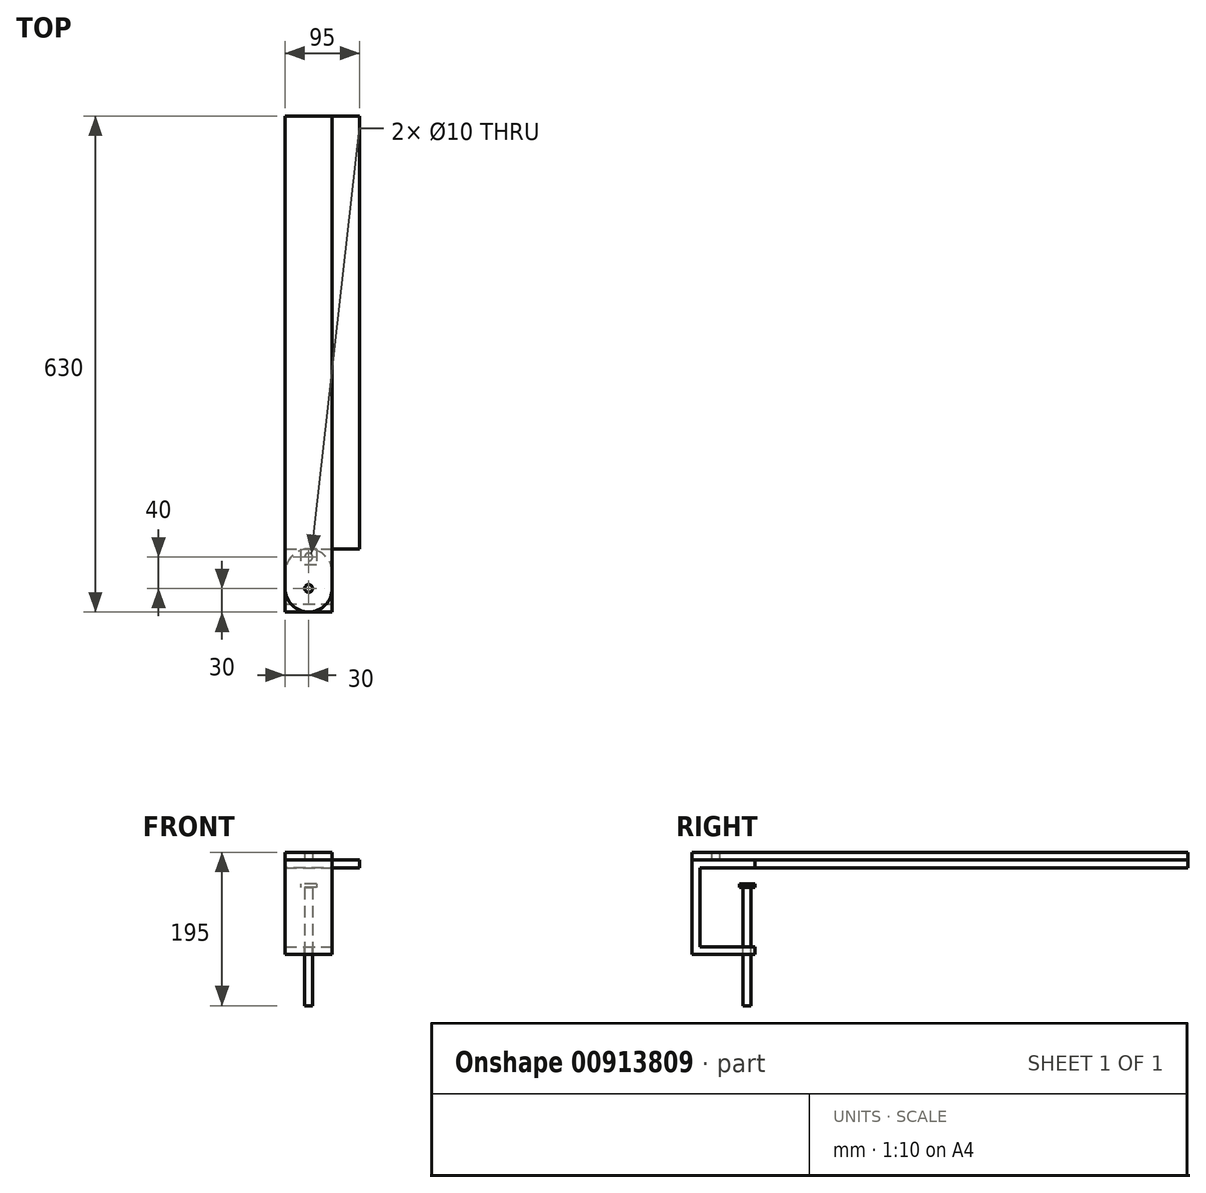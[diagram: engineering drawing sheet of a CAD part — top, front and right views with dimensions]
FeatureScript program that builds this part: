
annotation { "Feature Type Name" : "Feature", "Feature Type Description" : "" }
export const myFeature = defineFeature(function(context is Context, id is Id, definition is map)
    precondition{}
    {
        {
            assignVariable(context, id + "F0", {"name" : "espessura", "anyValue" : 10});
        }
        {
            var Q0;
            Q0=qCreatedBy(makeId("Top.planeOp"),FACE);
            var sketch = newSketch(context, id + "F1", { "sketchPlane" : qUnion([Q0])});
            skLineSegment(sketch, "E0.bottom", {"start": v(0, 0) * mm, "end": v(35, 0) * mm});
            skLineSegment(sketch, "E0.top", {"start": v(0, 550) * mm, "end": v(35, 550) * mm});
            skLineSegment(sketch, "E0.left", {"start": v(0, 0) * mm, "end": v(0, 550) * mm});
            skLineSegment(sketch, "E0.right", {"start": v(35, 0) * mm, "end": v(35, 550) * mm});
            skLineSegment(sketch, "E1.top", {"start": v(0, 550) * mm, "end": v(-60, 550) * mm});
            skLineSegment(sketch, "E1.right", {"start": v(-60, 0) * mm, "end": v(-60, 550) * mm});
            skLineSegment(sketch, "E2.top", {"start": v(-60, -50) * mm, "end": v(0, -50) * mm, "construction": true});
            skLineSegment(sketch, "E2.left", {"start": v(-60, 0) * mm, "end": v(-60, -50) * mm});
            skLineSegment(sketch, "E2.right", {"start": v(0, 0) * mm, "end": v(0, -50) * mm});
            skArc(sketch, "E3", {"start": v(-60, -50) * mm, "mid": v(-30, -80) * mm, "end": v(0, -50) * mm});
            skCircle(sketch, "E4", {"center": v(-30, -50) * mm, "radius": 5 * mm});
            skLineSegment(sketch, "E5", {"start": v(-60, 0) * mm, "end": v(0, 0) * mm});
            skSolve(sketch);
        }
        {
            var Q0;
            Q0=makeQuery(id+"F1.imprint","IMPRINT",FACE,{"disambiguationData":[TD([[makeQuery(id+"F1.imprint","IMPRINT",EDGE,{"derivedFrom":sQuery(id+"F1.wireOp",EDGE,"E1.top")}),1.0]])]});
            extrude(context, id + "F2", {"entities" : qUnion([Q0]), "depth" : (2 * getVariable(context, 'espessura')) * mm});
        }
        {
            var Q0;
            Q0=makeQuery(id+"F1.imprint","IMPRINT",FACE,{"disambiguationData":[TD([[makeQuery(id+"F1.imprint","IMPRINT",EDGE,{"derivedFrom":sQuery(id+"F1.wireOp",EDGE,"E0.bottom")}),1.0]])]});
            extrude(context, id + "F3", {"entities" : qUnion([Q0]), "operationType" : NewBodyOperationType.ADD, "depth" : (getVariable(context, 'espessura')) * mm});
        }
        {
            var Q0;
            Q0=makeQuery(id+"F1.imprint","IMPRINT",FACE,{"disambiguationData":[TD([[makeQuery(id+"F1.imprint","IMPRINT",EDGE,{"derivedFrom":sQuery(id+"F1.wireOp",EDGE,"E2.left")}),1.0]])]});
            extrude(context, id + "F4", {"entities" : qUnion([Q0]), "operationType" : NewBodyOperationType.ADD, "depth" : (2 * getVariable(context, 'espessura')) * mm});
        }
        {
            var Q0;
            Q0=makeQuery(id+"F1.imprint","IMPRINT",FACE,{"disambiguationData":[TD([[makeQuery(id+"F1.imprint","IMPRINT",EDGE,{"derivedFrom":sQuery(id+"F1.wireOp",EDGE,"E2.left")}),1.0]])]});
            extrude(context, id + "F5", {"entities" : qUnion([Q0]), "operationType" : NewBodyOperationType.REMOVE, "oppositeDirection" : true, "depth" : -(getVariable(context, 'espessura')) * mm});
        }
        {
            var Q0;
            {var subQ0=sQuery(id+"F1.wireOp",EDGE,"E5");var subQ1=sQuery(id+"F1.wireOp",EDGE,"E0.left");Q0=makeQuery(id+"F4.boolean.opBoolean","MERGE",FACE,{"derivedFrom":[makeQuery(id+"F3.boolean.opBoolean","MERGE",FACE,{"derivedFrom":[makeQuery(id+"F2.opExtrude","CAP_FACE",FACE,{"disambiguationData":[OSD([sQuery(id+"F1.wireOp",EDGE,"E1.top"),subQ1,sQuery(id+"F1.wireOp",EDGE,"E1.right"),subQ0])],"isStart":true}),makeQuery(id+"F3.opExtrude","CAP_FACE",FACE,{"disambiguationData":[OSD([sQuery(id+"F1.wireOp",EDGE,"E0.bottom"),sQuery(id+"F1.wireOp",EDGE,"E0.top"),sQuery(id+"F1.wireOp",EDGE,"E0.right"),subQ1])],"isStart":true})]}),makeQuery(id+"F4.opExtrude","CAP_FACE",FACE,{"disambiguationData":[OSD([sQuery(id+"F1.wireOp",EDGE,"E2.left"),sQuery(id+"F1.wireOp",EDGE,"E2.right"),sQuery(id+"F1.wireOp",EDGE,"E3"),sQuery(id+"F1.wireOp",EDGE,"E4"),subQ0])],"isStart":true})]});}
            var sketch = newSketch(context, id + "F6", { "sketchPlane" : qUnion([Q0])});
            skPoint(sketch, "E6.0", {"position": v(-60, 0) * mm});
            skPoint(sketch, "E7.0", {"position": v(0, 0) * mm});
            skLineSegment(sketch, "E8", {"start": v(-60, 0) * mm, "end": v(0, 0) * mm, "construction": true});
            skLineSegment(sketch, "E9", {"start": v(-30, 0) * mm, "end": v(-30, 30) * mm, "construction": true});
            skLineSegment(sketch, "E10", {"start": v(-60, 30) * mm, "end": v(-60, 30) * mm});
            skArc(sketch, "E11", {"start": v(-60, 30) * mm, "mid": v(-30, 0) * mm, "end": v(0, 30) * mm});
            skPoint(sketch, "E12.0", {"position": v(-30, 80) * mm});
            skPoint(sketch, "E13", {"position": v(-60, 30) * mm});
            skLineSegment(sketch, "E14.bottom", {"start": v(-60, 30) * mm, "end": v(0, 30) * mm, "construction": true});
            skLineSegment(sketch, "E14.top", {"start": v(-60, 80) * mm, "end": v(0, 80) * mm});
            skLineSegment(sketch, "E14.left", {"start": v(-60, 30) * mm, "end": v(-60, 80) * mm});
            skLineSegment(sketch, "E14.right", {"start": v(0, 30) * mm, "end": v(0, 80) * mm});
            skLineSegment(sketch, "E15", {"start": v(-60, 70) * mm, "end": v(0, 70) * mm});
            skSolve(sketch);
        }
        {
            var Q0;
            Q0=makeQuery(id+"F6.imprint","IMPRINT",FACE,{"disambiguationData":[TD([[makeQuery(id+"F6.imprint","IMPRINT",EDGE,{"derivedFrom":sQuery(id+"F6.wireOp",EDGE,"E14.top")}),-1.0]])]});
            var Q1;
            {var subQ3=sQuery(id+"F6.wireOp",EDGE,"E15");Q1=makeQuery(id+"F6.imprint","IMPRINT",FACE,{"disambiguationData":[TD([[makeQuery(id+"F6.imprint","IMPRINT",EDGE,{"derivedFrom":subQ3}),-1.0]])]});}
            extrude(context, id + "F7", {"entities" : qUnion([Q0, Q1]), "oppositeDirection" : true, "depth" : (getVariable(context, 'espessura')) * mm});
        }
        {
            var Q0;
            {var subQ0=sQuery(id+"F6.wireOp",EDGE,"E14.top");Q0=makeQuery(id+"F6.imprint","IMPRINT",FACE,{"disambiguationData":[TD([[makeQuery(id+"F6.imprint","IMPRINT",EDGE,{"derivedFrom":subQ0}),-1.0]])]});}
            extrude(context, id + "F8", {"entities" : qUnion([Q0]), "operationType" : NewBodyOperationType.ADD, "depth" : 100 * mm});
        }
        {
            var Q0;
            Q0=makeQuery(id+"F8.opExtrude","CAP_FACE",FACE,{"disambiguationData":[OSD([sQuery(id+"F6.wireOp",EDGE,"E14.top"),sQuery(id+"F6.wireOp",EDGE,"E14.left"),sQuery(id+"F6.wireOp",EDGE,"E14.right"),sQuery(id+"F6.wireOp",EDGE,"E15")])],"isStart":false});
            var sketch = newSketch(context, id + "F9", { "sketchPlane" : qUnion([Q0])});
            skLineSegment(sketch, "E16.0", {"start": v(-60, 80) * mm, "end": v(0, 80) * mm});
            skLineSegment(sketch, "E17.0.1", {"start": v(-60, 80) * mm, "end": v(-60, 70) * mm});
            skArc(sketch, "E17.0.2", {"start": v(-60, 30) * mm, "mid": v(-51.21, 8.79) * mm, "end": v(-30, 0) * mm});
            skArc(sketch, "E17.0.3", {"start": v(-30, 0) * mm, "mid": v(-8.79, 8.79) * mm, "end": v(0, 30) * mm});
            skLineSegment(sketch, "E17.0.4", {"start": v(0, 30) * mm, "end": v(0, 70) * mm});
            skLineSegment(sketch, "E18", {"start": v(-60, 80) * mm, "end": v(-60, 30) * mm});
            skLineSegment(sketch, "E19", {"start": v(0, 80) * mm, "end": v(0, 70) * mm});
            skLineSegment(sketch, "E20", {"start": v(-30, 0) * mm, "end": v(-30, 10) * mm, "construction": true});
            skCircle(sketch, "E21", {"center": v(-30, 10) * mm, "radius": 5 * mm});
            skSolve(sketch);
        }
        {
            var Q0;
            {var subQ2=sQuery(id+"F9.wireOp",EDGE,"E17.0.2");Q0=makeQuery(id+"F9.imprint","IMPRINT",FACE,{"disambiguationData":[TD([[makeQuery(id+"F9.imprint","IMPRINT",EDGE,{"derivedFrom":subQ2}),1.0]])]});}
            var Q1;
            {var subQ0=sQuery(id+"F9.wireOp",EDGE,"E16.0");Q1=makeQuery(id+"F9.imprint","IMPRINT",FACE,{"disambiguationData":[TD([[makeQuery(id+"F9.imprint","IMPRINT",EDGE,{"derivedFrom":subQ0}),-1.0]])]});}
            extrude(context, id + "F10", {"entities" : qUnion([Q0, Q1]), "operationType" : NewBodyOperationType.ADD, "depth" : (getVariable(context, 'espessura')) * mm});
        }
        {
            var Q0;
            Q0=makeQuery(id+"F10.opExtrude","CAP_FACE",FACE,{"disambiguationData":[OSD([sQuery(id+"F9.wireOp",EDGE,"E16.0"),sQuery(id+"F9.wireOp",EDGE,"E17.0.2"),sQuery(id+"F9.wireOp",EDGE,"E17.0.3"),sQuery(id+"F9.wireOp",EDGE,"E17.0.4"),sQuery(id+"F9.wireOp",EDGE,"E18"),sQuery(id+"F9.wireOp",EDGE,"E19"),sQuery(id+"F9.wireOp",EDGE,"E21")])],"isStart":true});
            var sketch = newSketch(context, id + "F11", { "sketchPlane" : qUnion([Q0])});
            skPoint(sketch, "E22.0", {"position": v(-30, 0) * mm});
            skLineSegment(sketch, "E23", {"start": v(-30, 0) * mm, "end": v(-30, -10) * mm, "construction": true});
            skCircle(sketch, "E24", {"center": v(-30, -10) * mm, "radius": 5 * mm});
            skSolve(sketch);
        }
        {
            var Q0;
            {var subQ0=sQuery(id+"F11.wireOp",EDGE,"E24");Q0=makeQuery(id+"F11.imprint","IMPRINT",FACE,{"disambiguationData":[TD([[makeQuery(id+"F11.imprint","IMPRINT",EDGE,{"disambiguationData":[OD(0.0)],"derivedFrom":subQ0}),-1.0]])]});}
            extrude(context, id + "F12", {"entities" : qUnion([Q0]), "depth" : 75 * mm, "hasSecondDirection" : true, "secondDirectionOppositeDirection" : true, "secondDirectionDepth" : 75 * mm});
        }
        {
            var Q0;
            Q0=makeQuery(id+"F12.opExtrude","CAP_FACE",FACE,{"disambiguationData":[OSD([sQuery(id+"F11.wireOp",EDGE,"E24")])],"isStart":false});
            var sketch = newSketch(context, id + "F13", { "sketchPlane" : qUnion([Q0])});
            skLineSegment(sketch, "E25", {"start": v(-25, -10) * mm, "end": v(-35, -10) * mm, "construction": true});
            skLineSegment(sketch, "E26", {"start": v(-30, -5) * mm, "end": v(-30, -15) * mm, "construction": true});
            skPoint(sketch, "E27", {"position": v(-30, -10) * mm});
            skLineSegment(sketch, "E28", {"start": v(-30, -5) * mm, "end": v(-30, 0) * mm, "construction": true});
            skLineSegment(sketch, "E29.bottom", {"start": v(-20, 0) * mm, "end": v(-40, 0) * mm});
            skLineSegment(sketch, "E29.top", {"start": v(-20, -20) * mm, "end": v(-40, -20) * mm});
            skLineSegment(sketch, "E29.left", {"start": v(-20, 0) * mm, "end": v(-20, -20) * mm});
            skLineSegment(sketch, "E29.right", {"start": v(-40, 0) * mm, "end": v(-40, -20) * mm});
            skSolve(sketch);
        }
        {
            var Q0;
            Q0=qSketchRegion(id+"F13",true);
            var Q1;
            Q1=makeQuery(id+"F13.imprint","IMPRINT",FACE,{"disambiguationData":[TD([[makeQuery(id+"F13.imprint","IMPRINT",EDGE,{"derivedFrom":sQuery(id+"F13.wireOp",EDGE,"E29.bottom")}),1.0]])]});
            extrude(context, id + "F14", {"entities" : qUnion([Q0, Q1]), "operationType" : NewBodyOperationType.ADD, "depth" : 5 * mm});
        }
    });
